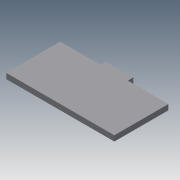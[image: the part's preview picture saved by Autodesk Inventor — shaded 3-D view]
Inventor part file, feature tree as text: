
AUTODESK INVENTOR PART (.ipt)
format: ipt  version: 2014 (Build 180170000, 170)  size: 75,264 bytes
history: native  units: mm
features: other x1, extrude x1, sketch x1
ambient origin geometry x8: Origin, YZ Plane, XZ Plane, XY Plane, X Axis, Y Axis, Z Axis, Center Point
bodies: Body1 (feature_tree)
feature tree (3):
  other  "ソリッド1"
  extrude  "押し出し1"  Depth=20.0mm
  sketch  "スケッチ1"
